FCSTD DOCUMENT  (FreeCAD 1.0R39319 (Git))
Label: Unnamed1
License: Yes
LicenseURL: https://en.wikipedia.org/wiki/Yes
objects: Part::FeaturePython×8, Part::Part2DObjectPython×4
note: 12 computed .brp shape members not serialized (recipe doc carries the construction recipe); baked Part::Feature solids carry a one-line shape summary decoded from their .brp

FEATURE [Part::FeaturePython] Point  label="A1"  # WARN: FeaturePython — macro-defined, semantics opaque (R4)
  X = 0
  Y = 0
  Z = 0
FEATURE [Part::FeaturePython] Point001  label="A2"  # WARN: FeaturePython — macro-defined, semantics opaque (R4)
  Placement = pos=(0,0,16.5) rot=(0,0,1;0rad)
  X = 0
  Y = 0
  Z = 16.5
FEATURE [Part::FeaturePython] Point002  label="D1"  # WARN: FeaturePython — macro-defined, semantics opaque (R4)
  Placement = pos=(100,0,0) rot=(0,0,1;0rad)
  X = 100
  Y = 0
  Z = 0
FEATURE [Part::FeaturePython] Point003  label="B1"  # WARN: FeaturePython — macro-defined, semantics opaque (R4)
  Placement = pos=(0,100,0) rot=(0,0,1;0rad)
  X = 0
  Y = 100
  Z = 0
FEATURE [Part::FeaturePython] Point004  label="C1"  # WARN: FeaturePython — macro-defined, semantics opaque (R4)
  Placement = pos=(100,100,0) rot=(0,0,1;0rad)
  X = 100
  Y = 100
  Z = 0
FEATURE [Part::FeaturePython] Point005  label="D2"  # WARN: FeaturePython — macro-defined, semantics opaque (R4)
  Placement = pos=(100,0,16.5) rot=(0,0,1;0rad)
  X = 100
  Y = 0
  Z = 16.5
FEATURE [Part::FeaturePython] Point006  label="B2"  # WARN: FeaturePython — macro-defined, semantics opaque (R4)
  Placement = pos=(0,100,16.5) rot=(0,0,1;0rad)
  X = 0
  Y = 100
  Z = 16.5
FEATURE [Part::FeaturePython] Point008  label="C2"  # WARN: FeaturePython — macro-defined, semantics opaque (R4)
  Placement = pos=(100,100,16.5) rot=(0,0,1;0rad)
  X = 100
  Y = 100
  Z = 16.5
FEATURE [Part::Part2DObjectPython] Line  # Draft 2D object (typed FeaturePython)
  Area = 0
  ChamferSize = 0
  Closed = false
  End = (0,0,16.5)
  FilletRadius = 0
  Length = 16.5
  MakeFace = false
  Points = (2) [(0,0,0),(0,0,16.5)]
  Start = (0,0,0)
  Subdivisions = 0
FEATURE [Part::Part2DObjectPython] Line001  # Draft 2D object (typed FeaturePython)
  Area = 0
  ChamferSize = 0
  Closed = false
  End = (0,100,16.5)
  FilletRadius = 0
  Length = 16.5
  MakeFace = false
  Points = (2) [(0,100,0),(0,100,16.5)]
  Start = (0,100,0)
  Subdivisions = 0
FEATURE [Part::Part2DObjectPython] Line002  # Draft 2D object (typed FeaturePython)
  Area = 0
  ChamferSize = 0
  Closed = false
  End = (100,100,16.5)
  FilletRadius = 0
  Length = 16.5
  MakeFace = false
  Points = (2) [(100,100,0),(100,100,16.5)]
  Start = (100,100,0)
  Subdivisions = 0
FEATURE [Part::Part2DObjectPython] Line003  # Draft 2D object (typed FeaturePython)
  Area = 0
  ChamferSize = 0
  Closed = false
  End = (100,0,16.5)
  FilletRadius = 0
  Length = 16.5
  MakeFace = false
  Points = (2) [(100,0,0),(100,0,16.5)]
  Start = (100,0,0)
  Subdivisions = 0
